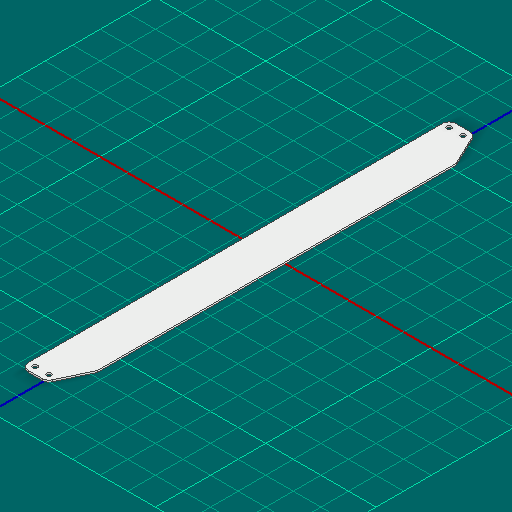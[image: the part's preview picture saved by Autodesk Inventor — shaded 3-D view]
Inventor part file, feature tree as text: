
AUTODESK INVENTOR PART (.ipt)
format: ipt  version: 2025 (Build 290162000, 162)  size: 115,200 bytes
history: native  units: in
note: dims shown in document units (in); Inventor stores cm internally (conversion verified against a paired STEP export)
features: extrude x1, sketch x1
ambient origin geometry x8: Origin, YZ Plane, XZ Plane, XY Plane, X Axis, Y Axis, Z Axis, Center Point
bodies: Solid1 (feature_tree)
feature tree (2):
  extrude  "Extrusion1"  Depth=0.0625in TaperAngle=0.0deg
  sketch  "Sketch1"  dims[d0=13.0in d1=0.0625in d2=0.0in]
